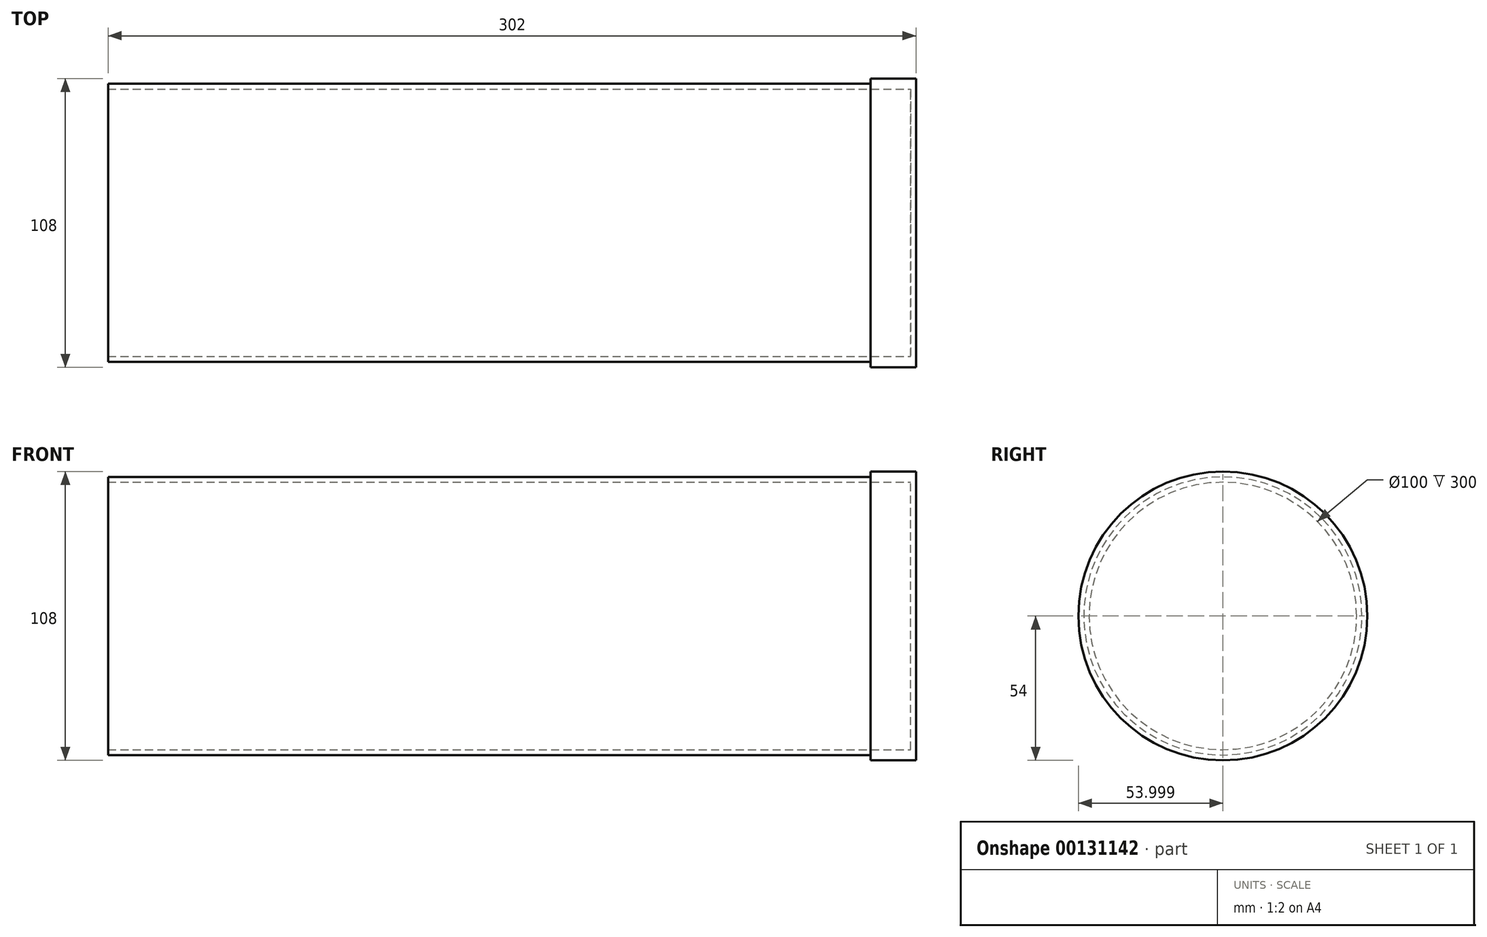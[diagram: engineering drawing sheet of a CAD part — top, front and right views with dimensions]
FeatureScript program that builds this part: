
annotation { "Feature Type Name" : "Feature", "Feature Type Description" : "" }
export const myFeature = defineFeature(function(context is Context, id is Id, definition is map)
    precondition{}
    {
        {
            assignVariable(context, id + "F0", {"name" : "length", "anyValue" : 300});
        }
        {
            assignVariable(context, id + "F1", {"name" : "hull_thickness", "anyValue" : 2});
        }
        {
            var Q0;
            Q0=qCreatedBy(makeId("Right.planeOp"),FACE);
            var sketch = newSketch(context, id + "F2", { "sketchPlane" : qUnion([Q0])});
            skCircle(sketch, "E0", {"center": v(-44.05, 36.4) * mm, "radius": 50 * mm});
            skCircle(sketch, "E1.0", {"center": v(-44.05, 36.4) * mm, "radius": 52 * mm});
            skSolve(sketch);
        }
        {
            var Q0;
            Q0=makeQuery(id+"F2.imprint","IMPRINT",FACE,{"disambiguationData":[TD([[makeQuery(id+"F2.imprint","IMPRINT",EDGE,{"derivedFrom":sQuery(id+"F2.wireOp",EDGE,"E0")}),-1.0]])]});
            extrude(context, id + "F3", {"entities" : qUnion([Q0]), "oppositeDirection" : true, "depth" : (getVariable(context, 'length')) * mm});
        }
        {
            assignVariable(context, id + "F4", {"name" : "cap_length", "anyValue" : 15});
        }
        {
            var Q0;
            Q0=makeQuery(id+"F3.opExtrude","CAP_FACE",FACE,{"disambiguationData":[OSD([sQuery(id+"F2.wireOp",EDGE,"E0"),sQuery(id+"F2.wireOp",EDGE,"E1.0")])],"isStart":true});
            var sketch = newSketch(context, id + "F5", { "sketchPlane" : qUnion([Q0])});
            skCircle(sketch, "E2.0", {"center": v(-44.05, 36.4) * mm, "radius": 54 * mm});
            skSolve(sketch);
        }
        {
            var Q0;
            Q0=makeQuery(id+"F5.imprint","IMPRINT",FACE,{"disambiguationData":[TD([[makeQuery(id+"F5.imprint","IMPRINT",EDGE,{"derivedFrom":sQuery(id+"F5.wireOp",EDGE,"E2.0")}),1.0]])]});
            extrude(context, id + "F6", {"entities" : qUnion([Q0]), "oppositeDirection" : true, "depth" : (getVariable(context, 'cap_length')) * mm});
        }
        {
            var Q0;
            Q0=makeQuery(id+"F5.imprint","IMPRINT",FACE,{"disambiguationData":[TD([[makeQuery(id+"F5.imprint","IMPRINT",EDGE,{"derivedFrom":makeQuery(id+"F3.opExtrude","CAP_EDGE",EDGE,{"disambiguationData":[OSD([sQuery(id+"F2.wireOp",EDGE,"E0")])],"isStart":true})}),-1.0]])]});
            var Q1;
            Q1=makeQuery(id+"F5.imprint","IMPRINT",FACE,{"disambiguationData":[TD([[makeQuery(id+"F5.imprint","IMPRINT",EDGE,{"derivedFrom":makeQuery(id+"F3.opExtrude","CAP_EDGE",EDGE,{"disambiguationData":[OSD([sQuery(id+"F2.wireOp",EDGE,"E0")])],"isStart":true})}),1.0]])]});
            var Q2;
            Q2=makeQuery(id+"F5.imprint","IMPRINT",FACE,{"disambiguationData":[TD([[makeQuery(id+"F5.imprint","IMPRINT",EDGE,{"derivedFrom":sQuery(id+"F5.wireOp",EDGE,"E2.0")}),1.0]])]});
            extrude(context, id + "F7", {"entities" : qUnion([Q0, Q1, Q2]), "operationType" : NewBodyOperationType.ADD, "depth" : (getVariable(context, 'hull_thickness')) * mm});
        }
    });
